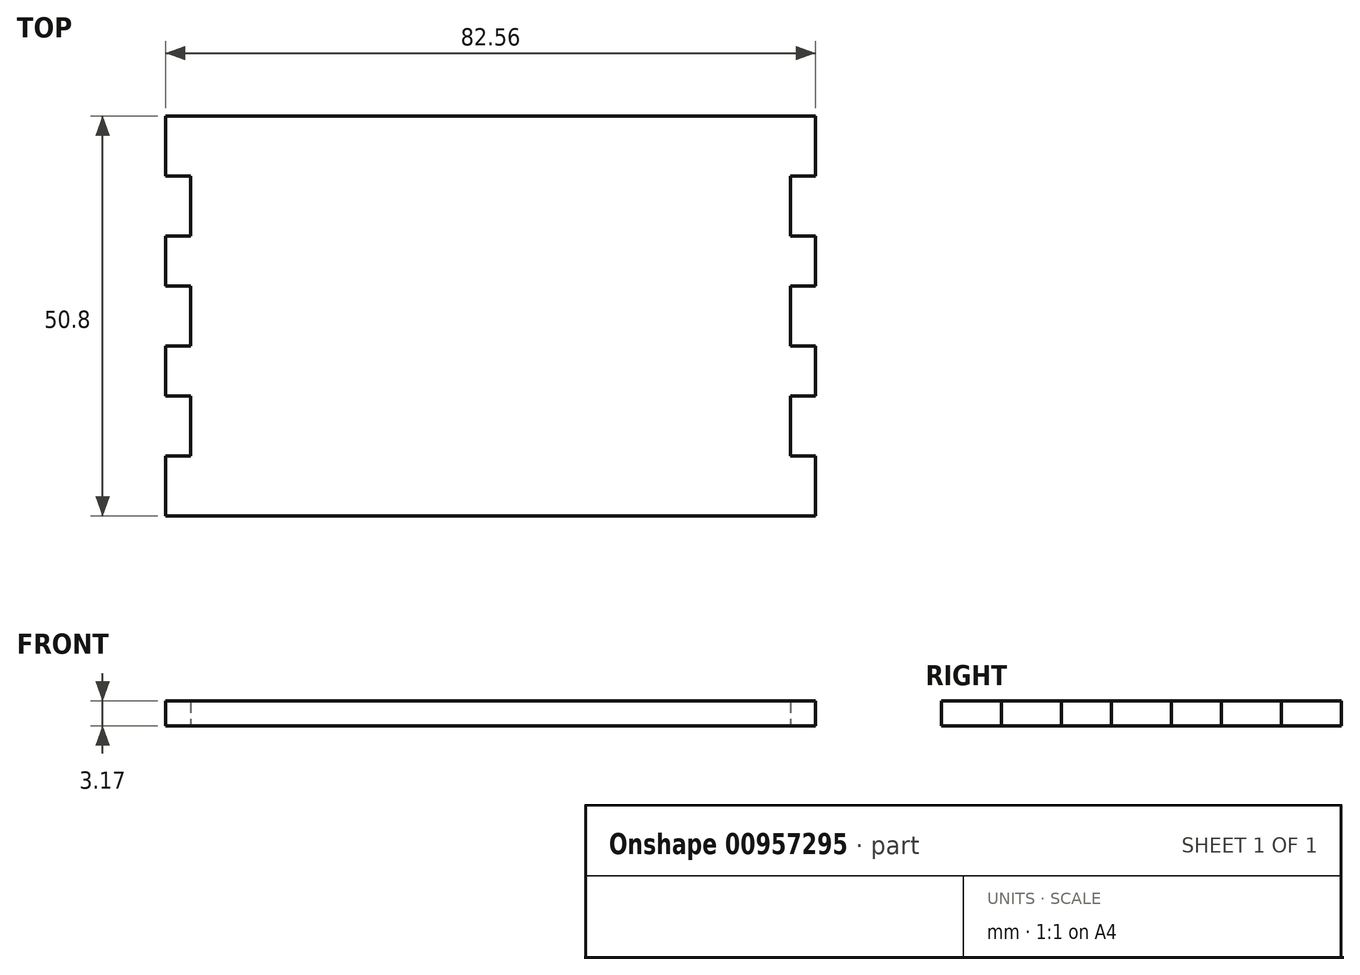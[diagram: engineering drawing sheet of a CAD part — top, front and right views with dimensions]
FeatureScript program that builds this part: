
annotation { "Feature Type Name" : "Feature", "Feature Type Description" : "" }
export const myFeature = defineFeature(function(context is Context, id is Id, definition is map)
    precondition{}
    {
        {
            var Q0;
            Q0=qCreatedBy(makeId("Top.planeOp"),FACE);
            var sketch = newSketch(context, id + "F0", { "sketchPlane" : qUnion([Q0])});
            skLineSegment(sketch, "E0", {"start": v(0, 0) * mm, "end": v(101.6, 0) * mm});
            skLineSegment(sketch, "E1", {"start": v(101.6, 0) * mm, "end": v(101.6, 7.62) * mm});
            skLineSegment(sketch, "E2", {"start": v(101.6, 7.62) * mm, "end": v(88.9, 7.62) * mm});
            skLineSegment(sketch, "E3", {"start": v(88.9, 7.62) * mm, "end": v(88.9, 15.24) * mm});
            skLineSegment(sketch, "E4", {"start": v(88.9, 15.24) * mm, "end": v(101.6, 15.24) * mm});
            skLineSegment(sketch, "E5", {"start": v(101.6, 15.24) * mm, "end": v(101.6, 21.59) * mm});
            skLineSegment(sketch, "E6", {"start": v(101.6, 21.59) * mm, "end": v(88.9, 21.59) * mm});
            skLineSegment(sketch, "E7", {"start": v(88.9, 21.59) * mm, "end": v(88.9, 29.21) * mm});
            skLineSegment(sketch, "E8", {"start": v(88.9, 29.21) * mm, "end": v(101.6, 29.21) * mm});
            skLineSegment(sketch, "E9", {"start": v(101.6, 29.21) * mm, "end": v(101.6, 35.56) * mm});
            skLineSegment(sketch, "E10", {"start": v(101.6, 35.56) * mm, "end": v(88.9, 35.56) * mm});
            skLineSegment(sketch, "E11", {"start": v(88.9, 35.56) * mm, "end": v(88.9, 43.18) * mm});
            skLineSegment(sketch, "E12", {"start": v(88.9, 43.18) * mm, "end": v(101.6, 43.18) * mm});
            skLineSegment(sketch, "E13", {"start": v(101.6, 43.18) * mm, "end": v(101.6, 50.8) * mm});
            skLineSegment(sketch, "E14", {"start": v(101.6, 50.8) * mm, "end": v(0, 50.8) * mm});
            skLineSegment(sketch, "E15", {"start": v(0, 50.8) * mm, "end": v(0, 42.54) * mm});
            skLineSegment(sketch, "E16.MirrorCS", {"start": v(0, 15.24) * mm, "end": v(0, 21.59) * mm});
            skLineSegment(sketch, "E17.MirrorCS", {"start": v(0, 29.21) * mm, "end": v(0, 35.56) * mm});
            skLineSegment(sketch, "E18.MirrorCS", {"start": v(0, 0) * mm, "end": v(0, 7.62) * mm});
            skLineSegment(sketch, "E19.MirrorCS", {"start": v(12.7, 21.59) * mm, "end": v(12.7, 29.21) * mm});
            skLineSegment(sketch, "E20.MirrorCS", {"start": v(0, 35.56) * mm, "end": v(12.7, 35.56) * mm});
            skLineSegment(sketch, "E21.MirrorCS", {"start": v(0, 21.59) * mm, "end": v(12.7, 21.59) * mm});
            skLineSegment(sketch, "E22.MirrorCS", {"start": v(0, 43.18) * mm, "end": v(0, 50.8) * mm});
            skLineSegment(sketch, "E23.MirrorCS", {"start": v(12.7, 43.18) * mm, "end": v(0, 43.18) * mm});
            skLineSegment(sketch, "E24.MirrorCS", {"start": v(12.7, 15.24) * mm, "end": v(0, 15.24) * mm});
            skLineSegment(sketch, "E25.MirrorCS", {"start": v(12.7, 7.62) * mm, "end": v(12.7, 15.24) * mm});
            skLineSegment(sketch, "E26.MirrorCS", {"start": v(12.7, 35.56) * mm, "end": v(12.7, 43.18) * mm});
            skLineSegment(sketch, "E27.MirrorCS", {"start": v(0, 7.62) * mm, "end": v(12.7, 7.62) * mm});
            skLineSegment(sketch, "E28.MirrorCS", {"start": v(12.7, 29.21) * mm, "end": v(0, 29.21) * mm});
            skPoint(sketch, "E29.end.orphan", {"position": v(50.8, 50.8) * mm});
            skPoint(sketch, "E29.start.orphan", {"position": v(50.8, 0) * mm});
            skSolve(sketch);
        }
        {
            var Q0;
            Q0=makeQuery(id+"F0.imprint","IMPRINT",FACE,{"disambiguationData":[TD([[makeQuery(id+"F0.imprint","IMPRINT",EDGE,{"derivedFrom":sQuery(id+"F0.wireOp",EDGE,"E0")}),1.0]])]});
            extrude(context, id + "F1", {"entities" : qUnion([Q0]), "depth" : 3.17 * mm, "offsetDistance" : 25.4 * mm});
        }
        {
            var Q0;
            Q0=makeQuery(id+"F1.opExtrude","SWEPT_FACE",FACE,{"disambiguationData":[OSD([sQuery(id+"F0.wireOp",EDGE,"E15")])]});
            var Q1;
            Q1=makeQuery(id+"F1.opExtrude","SWEPT_FACE",FACE,{"disambiguationData":[OSD([sQuery(id+"F0.wireOp",EDGE,"E17.MirrorCS")])]});
            var Q2;
            Q2=makeQuery(id+"F1.opExtrude","SWEPT_FACE",FACE,{"disambiguationData":[OSD([sQuery(id+"F0.wireOp",EDGE,"E16.MirrorCS")])]});
            var Q3;
            Q3=makeQuery(id+"F1.opExtrude","SWEPT_FACE",FACE,{"disambiguationData":[OSD([sQuery(id+"F0.wireOp",EDGE,"E18.MirrorCS")])]});
            extrude(context, id + "F2", {"entities" : qUnion([Q0, Q1, Q2, Q3]), "operationType" : NewBodyOperationType.REMOVE, "oppositeDirection" : true, "depth" : 9.52 * mm, "offsetDistance" : 25.4 * mm});
        }
        {
            var Q0;
            Q0=makeQuery(id+"F1.opExtrude","SWEPT_FACE",FACE,{"disambiguationData":[OSD([sQuery(id+"F0.wireOp",EDGE,"E1")])]});
            var Q1;
            Q1=makeQuery(id+"F1.opExtrude","SWEPT_FACE",FACE,{"disambiguationData":[OSD([sQuery(id+"F0.wireOp",EDGE,"E5")])]});
            var Q2;
            Q2=makeQuery(id+"F1.opExtrude","SWEPT_FACE",FACE,{"disambiguationData":[OSD([sQuery(id+"F0.wireOp",EDGE,"E9")])]});
            var Q3;
            Q3=makeQuery(id+"F1.opExtrude","SWEPT_FACE",FACE,{"disambiguationData":[OSD([sQuery(id+"F0.wireOp",EDGE,"E13")])]});
            extrude(context, id + "F3", {"entities" : qUnion([Q0, Q1, Q2, Q3]), "operationType" : NewBodyOperationType.REMOVE, "oppositeDirection" : true, "depth" : 9.52 * mm, "offsetDistance" : 25.4 * mm});
        }
    });
